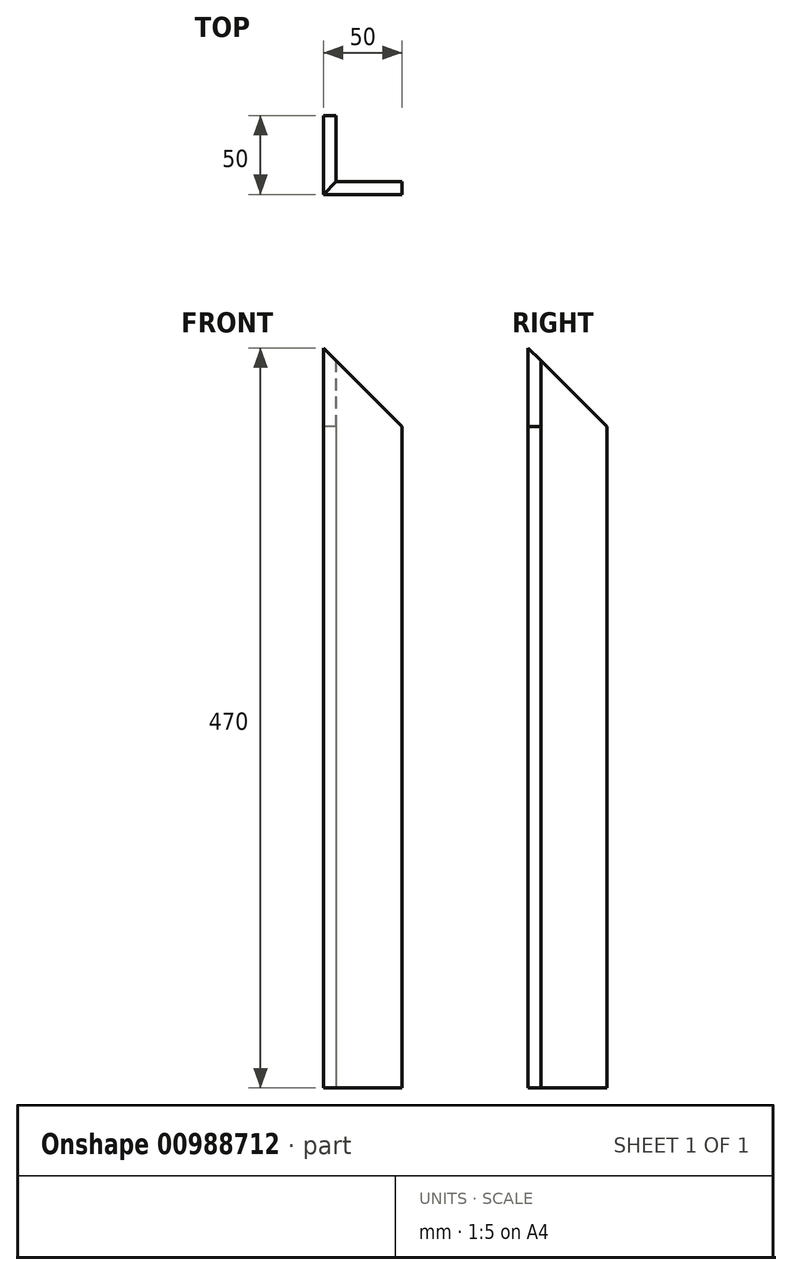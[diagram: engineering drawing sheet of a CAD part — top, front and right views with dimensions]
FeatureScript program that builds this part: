
annotation { "Feature Type Name" : "Feature", "Feature Type Description" : "" }
export const myFeature = defineFeature(function(context is Context, id is Id, definition is map)
    precondition{}
    {
        {
            var Q0;
            Q0=qCreatedBy(makeId("Top.planeOp"),FACE);
            var sketch = newSketch(context, id + "F0", { "sketchPlane" : qUnion([Q0])});
            skLineSegment(sketch, "E0", {"start": v(0, 0) * mm, "end": v(0, 50) * mm});
            skLineSegment(sketch, "E1", {"start": v(0, 50) * mm, "end": v(8, 50) * mm});
            skLineSegment(sketch, "E2", {"start": v(8, 50) * mm, "end": v(8, 8) * mm});
            skLineSegment(sketch, "E3", {"start": v(8, 8) * mm, "end": v(50, 8) * mm});
            skLineSegment(sketch, "E4", {"start": v(50, 8) * mm, "end": v(50, 0) * mm});
            skLineSegment(sketch, "E5", {"start": v(50, 0) * mm, "end": v(0, 0) * mm});
            skSolve(sketch);
        }
        {
            var Q0;
            Q0=qSketchRegion(id+"F0",true);
            extrude(context, id + "F1", {"entities" : qUnion([Q0]), "depth" : 470 * mm, "offsetDistance" : 25 * mm});
        }
        {
            var Q0;
            Q0=makeQuery(id+"F1.opExtrude","SWEPT_FACE",FACE,{"disambiguationData":[OSD([sQuery(id+"F0.wireOp",EDGE,"E5")])]});
            var sketch = newSketch(context, id + "F2", { "sketchPlane" : qUnion([Q0])});
            skLineSegment(sketch, "E6", {"start": v(0, 470) * mm, "end": v(50, 420) * mm});
            skLineSegment(sketch, "E7", {"start": v(50, 420) * mm, "end": v(50, 470) * mm});
            skLineSegment(sketch, "E8", {"start": v(50, 470) * mm, "end": v(0, 470) * mm});
            skSolve(sketch);
        }
        {
            var Q0;
            Q0=makeQuery(id+"F2.imprint","IMPRINT",FACE,{"disambiguationData":[TD([[makeQuery(id+"F2.imprint","IMPRINT",EDGE,{"derivedFrom":sQuery(id+"F2.wireOp",EDGE,"E6")}),1.0]])]});
            var Q1;
            Q1=makeQuery(id+"F1.opExtrude","SWEPT_FACE",FACE,{"disambiguationData":[OSD([sQuery(id+"F0.wireOp",EDGE,"E3")])]});
            extrude(context, id + "F3", {"entities" : qUnion([Q0]), "operationType" : NewBodyOperationType.REMOVE, "endBound" : BoundingType.UP_TO_SURFACE, "oppositeDirection" : true, "depth" : 25 * mm, "endBoundEntityFace" : qUnion([Q1]), "offsetDistance" : 25 * mm});
        }
        {
            var Q0;
            Q0=makeQuery(id+"F1.opExtrude","SWEPT_FACE",FACE,{"disambiguationData":[OSD([sQuery(id+"F0.wireOp",EDGE,"E0")])]});
            var sketch = newSketch(context, id + "F4", { "sketchPlane" : qUnion([Q0])});
            skLineSegment(sketch, "E9", {"start": v(0, 470) * mm, "end": v(0, 420) * mm});
            skLineSegment(sketch, "E10", {"start": v(0, 420) * mm, "end": v(-50, 420) * mm});
            skLineSegment(sketch, "E11", {"start": v(-50, 420) * mm, "end": v(0, 470) * mm});
            skSolve(sketch);
        }
        {
            var Q0;
            {var subQ0=sQuery(id+"F4.wireOp",EDGE,"E11");Q0=makeQuery(id+"F4.imprint","IMPRINT",FACE,{"disambiguationData":[TD([[makeQuery(id+"F4.imprint","IMPRINT",EDGE,{"derivedFrom":subQ0}),1.0]])]});}
            var Q1;
            Q1=makeQuery(id+"F1.opExtrude","SWEPT_FACE",FACE,{"disambiguationData":[OSD([sQuery(id+"F0.wireOp",EDGE,"E2")])]});
            extrude(context, id + "F5", {"entities" : qUnion([Q0]), "operationType" : NewBodyOperationType.REMOVE, "endBound" : BoundingType.UP_TO_SURFACE, "oppositeDirection" : true, "depth" : 25 * mm, "endBoundEntityFace" : qUnion([Q1]), "offsetDistance" : 25 * mm});
        }
    });
